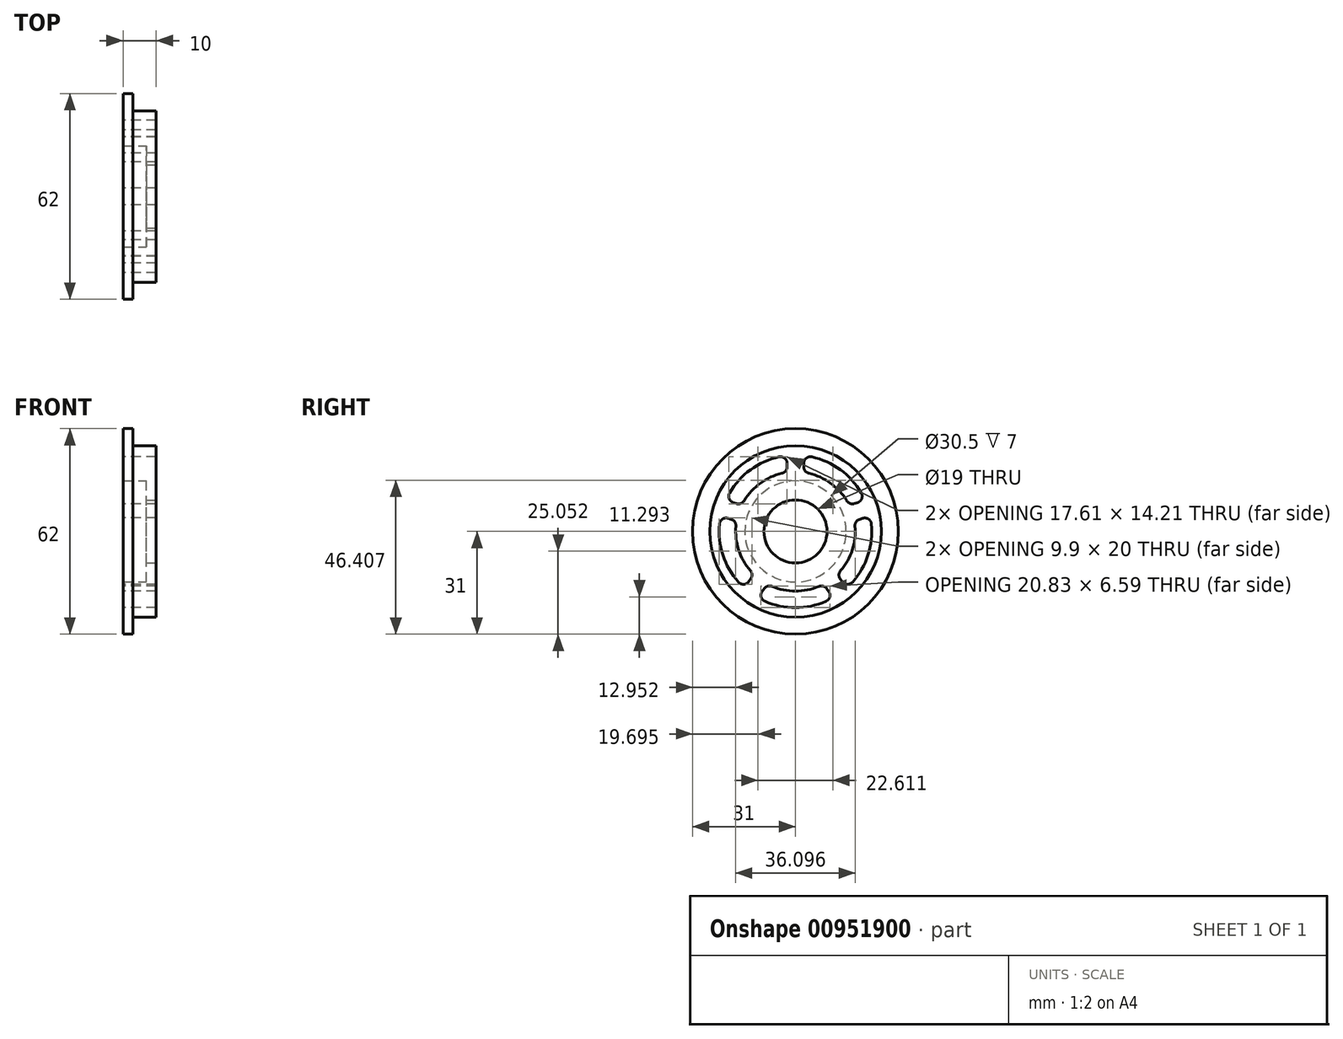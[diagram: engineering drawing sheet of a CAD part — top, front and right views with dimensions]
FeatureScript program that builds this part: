
annotation { "Feature Type Name" : "Feature", "Feature Type Description" : "" }
export const myFeature = defineFeature(function(context is Context, id is Id, definition is map)
    precondition{}
    {
        {
            var Q0;
            Q0=qCreatedBy(makeId("Top.planeOp"),FACE);
            var sketch = newSketch(context, id + "F0", { "sketchPlane" : qUnion([Q0])});
            skLineSegment(sketch, "E0", {"start": v(-3.83, 15.25) * mm, "end": v(-3.83, 31) * mm});
            skLineSegment(sketch, "E1", {"start": v(-3.83, 31) * mm, "end": v(-0.83, 31) * mm});
            skLineSegment(sketch, "E2", {"start": v(-0.83, 31) * mm, "end": v(-0.83, 25.85) * mm});
            skLineSegment(sketch, "E3", {"start": v(-0.83, 25.85) * mm, "end": v(6.17, 25.85) * mm});
            skLineSegment(sketch, "E4", {"start": v(6.17, 25.85) * mm, "end": v(6.17, 9.5) * mm});
            skLineSegment(sketch, "E5", {"start": v(6.17, 0) * mm, "end": v(3.17, 0) * mm});
            skLineSegment(sketch, "E6", {"start": v(-3.83, 15.25) * mm, "end": v(3.17, 15.25) * mm});
            skLineSegment(sketch, "E7", {"start": v(3.17, 15.25) * mm, "end": v(3.17, 9.5) * mm});
            skPoint(sketch, "E8.orphan", {"position": v(-3.83, 0) * mm});
            skLineSegment(sketch, "E9", {"start": v(3.17, 9.5) * mm, "end": v(6.17, 9.5) * mm});
            skLineSegment(sketch, "E10", {"start": v(-19.5, 0) * mm, "end": v(20.08, 0) * mm, "construction": true});
            skSolve(sketch);
        }
        {
            var Q0;
            Q0=makeQuery(id+"F0.imprint","IMPRINT",FACE,{"disambiguationData":[TD([[makeQuery(id+"F0.imprint","IMPRINT",EDGE,{"derivedFrom":sQuery(id+"F0.wireOp",EDGE,"E0")}),-1.0]])]});
            var Q1;
            Q1=sQuery(id+"F0.wireOp",EDGE,"E5");
            revolve(context, id + "F1", {"surfaceOperationType" : NewSurfaceOperationType.NEW, "entities" : qUnion([Q0]), "axis" : qUnion([Q1]), "revolveType" : RevolveType.FULL});
        }
        {
            var Q0;
            Q0=makeQuery(id+"F1.opRevolve","SWEPT_FACE",FACE,{"disambiguationData":[OSD([sQuery(id+"F0.wireOp",EDGE,"E0")])]});
            var sketch = newSketch(context, id + "F2", { "sketchPlane" : qUnion([Q0])});
            skArc(sketch, "E11", {"start": v(-4.93, 22.47) * mm, "mid": v(-13.52, 18.6) * mm, "end": v(-19.84, 11.63) * mm});
            skArc(sketch, "E12", {"start": v(-4.05, 17.54) * mm, "mid": v(-10.58, 14.56) * mm, "end": v(-15.43, 9.27) * mm});
            skLineSegment(sketch, "E13", {"start": v(0, 0) * mm, "end": v(0, 39.65) * mm, "construction": true});
            skLineSegment(sketch, "E14", {"start": v(0, 0) * mm, "end": v(40.54, 13.17) * mm, "construction": true});
            skLineSegment(sketch, "E15", {"start": v(0, 0) * mm, "end": v(-40.17, 13.05) * mm, "construction": true});
            skLineSegment(sketch, "E16", {"start": v(0, 0) * mm, "end": v(21.69, -29.85) * mm, "construction": true});
            skLineSegment(sketch, "E17", {"start": v(0, 0) * mm, "end": v(-24.37, -33.54) * mm, "construction": true});
            skLineSegment(sketch, "E18", {"start": v(-2.5, 20.51) * mm, "end": v(-2.5, 19.49) * mm});
            skLineSegment(sketch, "E19", {"start": v(2.5, 20.51) * mm, "end": v(2.5, 19.49) * mm});
            skLineSegment(sketch, "E20", {"start": v(18.74, 8.72) * mm, "end": v(17.76, 8.4) * mm});
            skLineSegment(sketch, "E21", {"start": v(20.28, 3.96) * mm, "end": v(19.3, 3.64) * mm});
            skLineSegment(sketch, "E22", {"start": v(10.03, -18.06) * mm, "end": v(9.43, -17.23) * mm});
            skLineSegment(sketch, "E23", {"start": v(-10.03, -18.06) * mm, "end": v(-9.43, -17.23) * mm});
            skLineSegment(sketch, "E24", {"start": v(-14.08, -15.13) * mm, "end": v(-13.48, -14.3) * mm});
            skLineSegment(sketch, "E25", {"start": v(-20.28, 3.96) * mm, "end": v(-19.3, 3.64) * mm});
            skLineSegment(sketch, "E26", {"start": v(-18.74, 8.72) * mm, "end": v(-17.76, 8.4) * mm});
            skLineSegment(sketch, "E27", {"start": v(13.48, -14.3) * mm, "end": v(14.08, -15.13) * mm});
            skArc(sketch, "E28.trimOffspring", {"start": v(19.84, 11.63) * mm, "mid": v(13.52, 18.6) * mm, "end": v(4.93, 22.47) * mm});
            skArc(sketch, "E29.trimOffspring", {"start": v(15.43, 9.27) * mm, "mid": v(10.58, 14.56) * mm, "end": v(4.05, 17.54) * mm});
            skArc(sketch, "E30.trimOffspring", {"start": v(13.59, -11.8) * mm, "mid": v(17.12, -5.56) * mm, "end": v(17.93, 1.57) * mm});
            skArc(sketch, "E31.trimOffspring", {"start": v(17.2, -15.28) * mm, "mid": v(21.87, -7.1) * mm, "end": v(22.89, 2.25) * mm});
            skArc(sketch, "E32.trimOffspring", {"start": v(-7.03, -16.57) * mm, "mid": v(0, -18) * mm, "end": v(7.03, -16.57) * mm});
            skArc(sketch, "E33.trimOffspring", {"start": v(-9.22, -21.07) * mm, "mid": v(0, -23) * mm, "end": v(9.22, -21.07) * mm});
            skArc(sketch, "E34.trimOffspring", {"start": v(-17.93, 1.57) * mm, "mid": v(-17.12, -5.56) * mm, "end": v(-13.59, -11.8) * mm});
            skArc(sketch, "E35.trimOffspring", {"start": v(-22.89, 2.25) * mm, "mid": v(-21.87, -7.1) * mm, "end": v(-17.2, -15.28) * mm});
            skPoint(sketch, "E36.visualSharp", {"position": v(-20.97, 9.44) * mm});
            skArc(sketch, "E36.filletArc", {"start": v(-19.84, 11.63) * mm, "mid": v(-19.99, 9.9) * mm, "end": v(-18.74, 8.72) * mm});
            skPoint(sketch, "E37.visualSharp", {"position": v(-16.18, 7.89) * mm});
            skArc(sketch, "E37.filletArc", {"start": v(-17.76, 8.4) * mm, "mid": v(-16.44, 8.43) * mm, "end": v(-15.43, 9.27) * mm});
            skPoint(sketch, "E38.visualSharp", {"position": v(-2.5, 22.86) * mm});
            skArc(sketch, "E38.filletArc", {"start": v(-2.5, 20.51) * mm, "mid": v(-3.25, 22.07) * mm, "end": v(-4.93, 22.47) * mm});
            skPoint(sketch, "E39.visualSharp", {"position": v(-2.5, 17.83) * mm});
            skArc(sketch, "E39.filletArc", {"start": v(-4.05, 17.54) * mm, "mid": v(-2.93, 18.24) * mm, "end": v(-2.5, 19.49) * mm});
            skPoint(sketch, "E40.visualSharp", {"position": v(2.5, 22.86) * mm});
            skArc(sketch, "E40.filletArc", {"start": v(4.93, 22.47) * mm, "mid": v(3.25, 22.07) * mm, "end": v(2.5, 20.51) * mm});
            skPoint(sketch, "E41.visualSharp", {"position": v(2.5, 17.83) * mm});
            skArc(sketch, "E41.filletArc", {"start": v(2.5, 19.49) * mm, "mid": v(2.93, 18.24) * mm, "end": v(4.05, 17.54) * mm});
            skPoint(sketch, "E42.visualSharp", {"position": v(20.97, 9.44) * mm});
            skArc(sketch, "E42.filletArc", {"start": v(18.74, 8.72) * mm, "mid": v(19.99, 9.9) * mm, "end": v(19.84, 11.63) * mm});
            skPoint(sketch, "E43.visualSharp", {"position": v(16.18, 7.89) * mm});
            skArc(sketch, "E43.filletArc", {"start": v(15.43, 9.27) * mm, "mid": v(16.44, 8.43) * mm, "end": v(17.76, 8.4) * mm});
            skPoint(sketch, "E44.visualSharp", {"position": v(17.73, 3.13) * mm});
            skArc(sketch, "E44.filletArc", {"start": v(19.3, 3.64) * mm, "mid": v(18.26, 2.85) * mm, "end": v(17.93, 1.57) * mm});
            skPoint(sketch, "E45.visualSharp", {"position": v(22.52, 4.69) * mm});
            skArc(sketch, "E45.filletArc", {"start": v(22.89, 2.25) * mm, "mid": v(22, 3.73) * mm, "end": v(20.28, 3.96) * mm});
            skPoint(sketch, "E46.visualSharp", {"position": v(12.5, -12.95) * mm});
            skArc(sketch, "E46.filletArc", {"start": v(13.59, -11.8) * mm, "mid": v(13.1, -13.03) * mm, "end": v(13.48, -14.3) * mm});
            skPoint(sketch, "E47.visualSharp", {"position": v(15.46, -17.03) * mm});
            skArc(sketch, "E47.filletArc", {"start": v(14.08, -15.13) * mm, "mid": v(15.6, -15.95) * mm, "end": v(17.2, -15.28) * mm});
            skPoint(sketch, "E48.visualSharp", {"position": v(8.46, -15.9) * mm});
            skArc(sketch, "E48.filletArc", {"start": v(9.43, -17.23) * mm, "mid": v(8.35, -16.48) * mm, "end": v(7.03, -16.57) * mm});
            skPoint(sketch, "E49.visualSharp", {"position": v(11.42, -19.97) * mm});
            skArc(sketch, "E49.filletArc", {"start": v(9.22, -21.07) * mm, "mid": v(10.35, -19.76) * mm, "end": v(10.03, -18.06) * mm});
            skPoint(sketch, "E50.visualSharp", {"position": v(-8.46, -15.9) * mm});
            skArc(sketch, "E50.filletArc", {"start": v(-7.03, -16.57) * mm, "mid": v(-8.35, -16.48) * mm, "end": v(-9.43, -17.23) * mm});
            skPoint(sketch, "E51.visualSharp", {"position": v(-11.42, -19.97) * mm});
            skArc(sketch, "E51.filletArc", {"start": v(-10.03, -18.06) * mm, "mid": v(-10.35, -19.76) * mm, "end": v(-9.22, -21.07) * mm});
            skPoint(sketch, "E52.visualSharp", {"position": v(-12.5, -12.95) * mm});
            skArc(sketch, "E52.filletArc", {"start": v(-13.48, -14.3) * mm, "mid": v(-13.1, -13.03) * mm, "end": v(-13.59, -11.8) * mm});
            skPoint(sketch, "E53.visualSharp", {"position": v(-15.46, -17.03) * mm});
            skArc(sketch, "E53.filletArc", {"start": v(-17.2, -15.28) * mm, "mid": v(-15.6, -15.95) * mm, "end": v(-14.08, -15.13) * mm});
            skPoint(sketch, "E54.visualSharp", {"position": v(-22.52, 4.69) * mm});
            skArc(sketch, "E54.filletArc", {"start": v(-20.28, 3.96) * mm, "mid": v(-22, 3.73) * mm, "end": v(-22.89, 2.25) * mm});
            skPoint(sketch, "E55.visualSharp", {"position": v(-17.73, 3.13) * mm});
            skArc(sketch, "E55.filletArc", {"start": v(-17.93, 1.57) * mm, "mid": v(-18.26, 2.85) * mm, "end": v(-19.3, 3.64) * mm});
            skSolve(sketch);
        }
        {
            var Q0;
            Q0=makeQuery(id+"F2.imprint","IMPRINT",FACE,{"disambiguationData":[TD([[makeQuery(id+"F2.imprint","IMPRINT",EDGE,{"derivedFrom":sQuery(id+"F2.wireOp",EDGE,"E11")}),1.0]])]});
            var Q1;
            Q1=makeQuery(id+"F2.imprint","IMPRINT",FACE,{"disambiguationData":[TD([[makeQuery(id+"F2.imprint","IMPRINT",EDGE,{"derivedFrom":sQuery(id+"F2.wireOp",EDGE,"E19")}),1.0]])]});
            var Q2;
            Q2=makeQuery(id+"F2.imprint","IMPRINT",FACE,{"disambiguationData":[TD([[makeQuery(id+"F2.imprint","IMPRINT",EDGE,{"derivedFrom":sQuery(id+"F2.wireOp",EDGE,"E21")}),1.0]])]});
            var Q3;
            Q3=makeQuery(id+"F2.imprint","IMPRINT",FACE,{"disambiguationData":[TD([[makeQuery(id+"F2.imprint","IMPRINT",EDGE,{"derivedFrom":sQuery(id+"F2.wireOp",EDGE,"E22")}),1.0]])]});
            var Q4;
            Q4=makeQuery(id+"F2.imprint","IMPRINT",FACE,{"disambiguationData":[TD([[makeQuery(id+"F2.imprint","IMPRINT",EDGE,{"derivedFrom":sQuery(id+"F2.wireOp",EDGE,"E24")}),1.0]])]});
            extrude(context, id + "F3", {"entities" : qUnion([Q0, Q1, Q2, Q3, Q4]), "operationType" : NewBodyOperationType.REMOVE, "oppositeDirection" : true, "depth" : 25 * mm, "offsetDistance" : 25 * mm});
        }
    });
